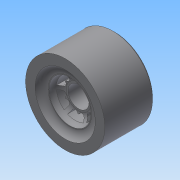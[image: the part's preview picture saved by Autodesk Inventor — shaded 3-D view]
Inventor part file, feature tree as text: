
AUTODESK INVENTOR PART (.ipt)
format: ipt  version: 2015 (Build 190159000, 159)  size: 289,792 bytes
history: native  units: in
note: dims shown in document units (in); Inventor stores cm internally (conversion verified against a paired STEP export)
features: extrude x4, fillet x4, sketch x1, other x1, chamfer x1
ambient origin geometry x8: Origin, YZ Plane, XZ Plane, XY Plane, X Axis, Y Axis, Z Axis, Center Point
bodies: Solid1 (feature_tree)
feature tree (11):
  sketch  "Sketch1"  dims[d0=3.2677in d1=0.3937in d2=0.315in d3=0.8661in d4=2.0472in d5=0.0in d6=1.6535in d7=0.0in d8=0.9449in d9=0.0in d10=0.3937in d11=1.7323in d14=60.0deg d15=2.3622in d17=360.0deg d19=0.3543in d20=0.8661in d21=0.0in d23=0.0787in d24=0.0787in d25=0.0787in d26=45.0deg d27=0.4331in d28=0.3543in]
  extrude  "Outside"  Depth=0.3937in
  extrude  "Middle"  Depth=0.3937in
  extrude  "Inside"  Depth=0.3937in
  fillet  "outside-outer fillet"  Radius=2.0472in
  other  "spokes"
  fillet  "outside-spoke fillet"  Radius=1.6535in
  chamfer  "inside-edge chamfer"  Distance=0.9449in
  fillet  "inside-outer fillet"  Radius=0.3937in
  fillet  "inside-spoke fillet"  Radius=1.7323in
  extrude  "spoke cutouts"  TaperAngle=60.0deg  [1 undecoded]
note: 1 required parameter value undecoded (feature->parameter linkage not recoverable at this tier; creation-order binding heuristic only, values carry confidence <= 0.55)
